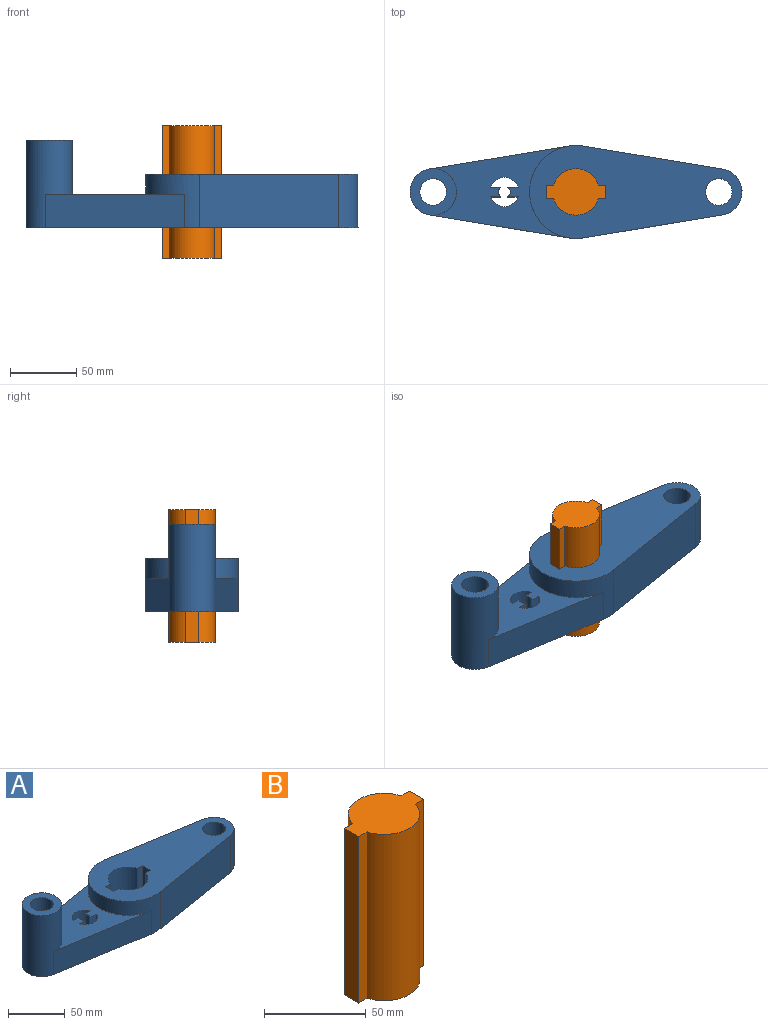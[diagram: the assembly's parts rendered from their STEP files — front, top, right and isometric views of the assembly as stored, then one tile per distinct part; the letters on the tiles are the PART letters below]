
ASSEMBLY  parts=2 mates=1
PART A: 29 faces, bbox 250x70x65.9 mm
  f0: cylinder r=35mm len=70mm, axis (0,0,-1), area 2393.3mm2, adj f8,f9,f13,f14,f22,f23,f25
  f1: cylinder r=17.5mm len=40mm, axis (0,0,-1), area 1793.5mm2, adj f2,f12,f13,f14
  f2: plane 40x5.73mm, normal (0,1,0), area 229.2mm2, adj f1,f3,f13,f14
  f3: plane 40x10mm, normal (1,0,0), area 400mm2, adj f2,f4,f13,f14
  f4: plane 40x5.73mm, normal (0,-1,0), area 229.2mm2, adj f3,f5,f13,f14
  f5: cylinder r=17.5mm len=40mm, axis (0,0,-1), area 1793.5mm2, adj f4,f6,f13,f14
  f6: plane 40x5.73mm, normal (0,-1,0), area 229.2mm2, adj f5,f7,f13,f14
  f7: plane 40x10mm, normal (-1,0,0), area 400mm2, adj f6,f12,f13,f14
  f8: plane 104.65x40mm, normal (0.16,0.99,0), area 4242.6mm2, adj f0,f11,f13,f14
  f9: plane 104.65x40mm, normal (0.16,-0.99,0), area 4242.6mm2, adj f0,f11,f13,f14
  f10: cylinder r=10mm len=40mm, axis (0,0,-1), area 2513.3mm2, adj f13,f14
  f11: cylinder r=17.5mm len=40mm, axis (0,0,-1), area 1970.2mm2, adj f8,f9,f13,f14
  f12: plane 40x5.73mm, normal (0,1,0), area 229.2mm2, adj f1,f7,f13,f14
  f13: plane 160x70mm, normal (0,0,1), area 6742.9mm2, adj f0,f1,f2,f3,f4,f5,f6,f7
  f14: plane 250x70mm, normal (0,0,-1), area 10425.4mm2, adj f0,f1,f2,f3,f4,f5,f6,f7
  f15: plane 25x7.85mm, normal (0,1,0), area 196.3mm2, adj f14,f16,f24,f25
  f16: cylinder r=4.5mm len=25mm, axis (0,0,-1), area 219.6mm2, adj f14,f15,f17,f25
  f17: plane 25x7.85mm, normal (0,-1,0), area 196.3mm2, adj f14,f16,f18,f25
  f18: cylinder r=11.02mm len=25mm, axis (0,0,-1), area 675.6mm2, adj f14,f17,f19,f25
  f19: plane 25x7.85mm, normal (0,-1,0), area 196.3mm2, adj f14,f18,f20,f25
  f20: cylinder r=4.5mm len=25mm, axis (0,0,-1), area 219.6mm2, adj f14,f19,f21,f25
  f21: plane 25x7.85mm, normal (0,1,0), area 196.3mm2, adj f14,f20,f24,f25
  f22: plane 104.65x25mm, normal (-0.16,0.99,0), area 2651.7mm2, adj f0,f14,f25,f26
  f23: plane 104.65x25mm, normal (-0.16,-0.99,0), area 2651.7mm2, adj f0,f14,f25,f26
  f24: cylinder r=11.02mm len=25mm, axis (0,0,-1), area 675.6mm2, adj f14,f15,f21,f25
  f25: plane 104.65x69.07mm, normal (0,0,1), area 3034.5mm2, adj f0,f15,f16,f17,f18,f19,f20,f21
  f26: cylinder r=17.5mm len=65.9mm, axis (0,0,-1), area 5728.6mm2, adj f14,f22,f23,f25,f28
  f27: cylinder r=10mm len=65.9mm, axis (0,0,-1), area 4140.6mm2, adj f14,f28
  f28: plane 35x35mm, normal (0,0,1), area 648mm2, adj f26,f27
PART B: 10 faces, bbox 45x35x100 mm
  f0: cylinder r=17.5mm len=100mm, axis (0,0,-1), area 4483.7mm2, adj f1,f7,f8,f9
  f1: plane 100x5.73mm, normal (0,-1,0), area 572.9mm2, adj f0,f2,f8,f9
  f2: plane 100x10mm, normal (1,0,0), area 1000mm2, adj f1,f3,f8,f9
  f3: plane 100x5.73mm, normal (0,1,0), area 572.9mm2, adj f2,f4,f8,f9
  f4: cylinder r=17.5mm len=100mm, axis (0,0,-1), area 4483.7mm2, adj f3,f5,f8,f9
  f5: plane 100x5.73mm, normal (0,1,0), area 572.9mm2, adj f4,f6,f8,f9
  f6: plane 100x10mm, normal (-1,0,0), area 1000mm2, adj f5,f7,f8,f9
  f7: plane 100x5.73mm, normal (0,-1,0), area 572.9mm2, adj f0,f6,f8,f9
  f8: plane 45x35mm, normal (0,0,1), area 1066.9mm2, adj f0,f1,f2,f3,f4,f5,f6,f7
  f9: plane 45x35mm, normal (0,0,-1), area 1066.9mm2, adj f0,f1,f2,f3,f4,f5,f6,f7
PLACE A t=(29.31,58.31,16.15)mm
PLACE B t=(29.31,58.31,42.92)mm
MATE slider B.f4 <-> A.f1  axis (0,0,1) through (29.31,58.31,92.92)mm
